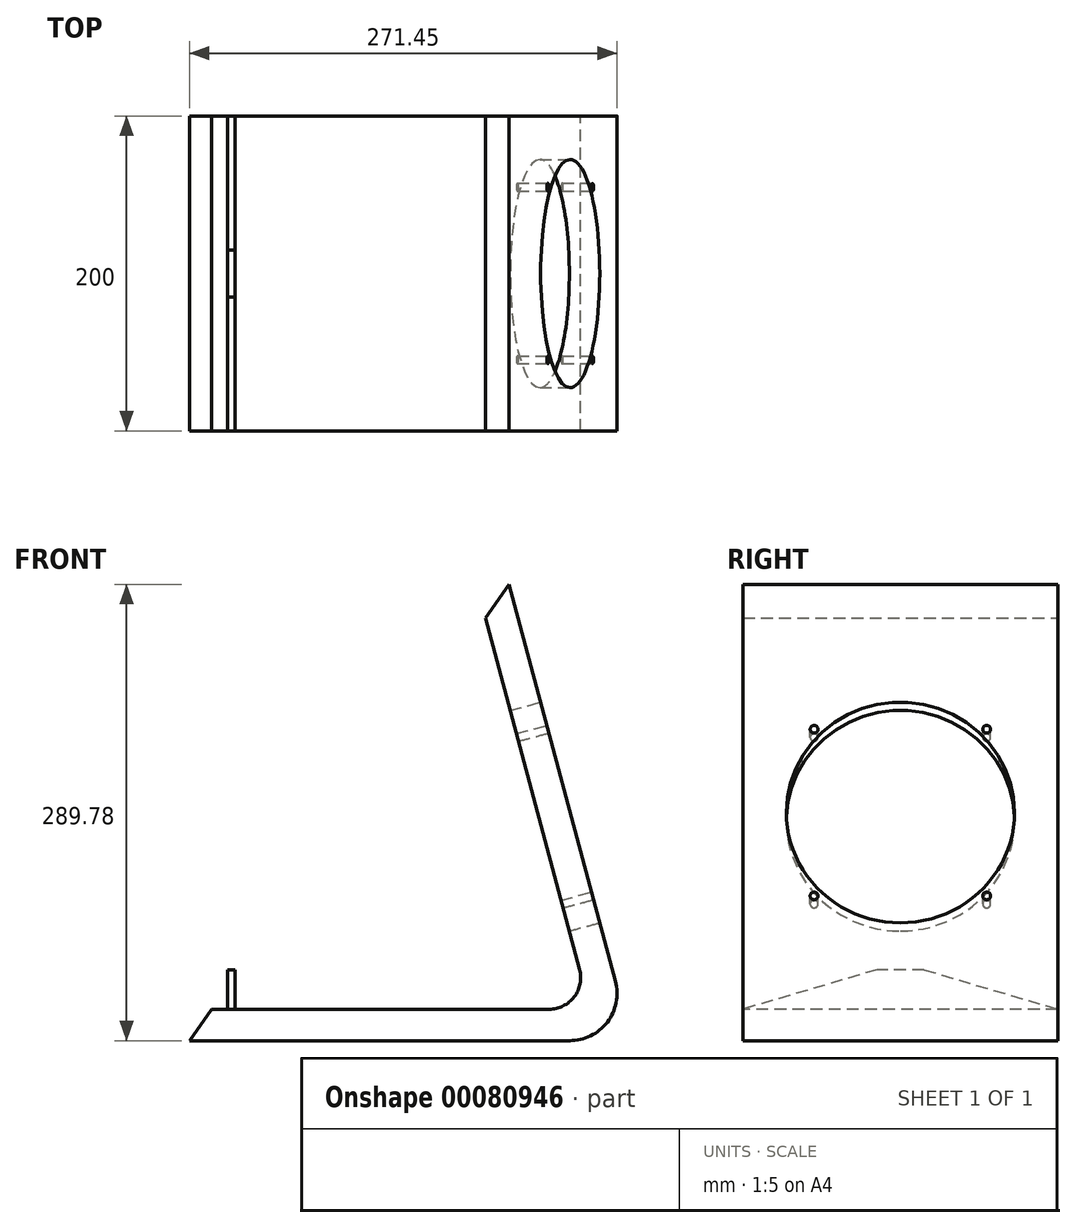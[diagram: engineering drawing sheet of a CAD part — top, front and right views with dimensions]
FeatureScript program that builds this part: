
annotation { "Feature Type Name" : "Feature", "Feature Type Description" : "" }
export const myFeature = defineFeature(function(context is Context, id is Id, definition is map)
    precondition{}
    {
        {
            var Q0;
            Q0=qCreatedBy(makeId("Front.planeOp"),FACE);
            var sketch = newSketch(context, id + "F0", { "sketchPlane" : qUnion([Q0])});
            skLineSegment(sketch, "E0", {"start": v(0, 0) * mm, "end": v(280.55, 0) * mm});
            skLineSegment(sketch, "E1", {"start": v(14, 20) * mm, "end": v(0, 0) * mm});
            skLineSegment(sketch, "E2", {"start": v(187.93, 268.4) * mm, "end": v(202.9, 289.78) * mm});
            skLineSegment(sketch, "E3", {"start": v(202.9, 289.78) * mm, "end": v(280.55, 0) * mm});
            skLineSegment(sketch, "E4", {"start": v(14, 20) * mm, "end": v(254.49, 20) * mm});
            skLineSegment(sketch, "E5", {"start": v(187.93, 268.4) * mm, "end": v(254.49, 20) * mm});
            skSolve(sketch);
        }
        {
            var Q0;
            Q0 = qSketchRegion(id + "F0", true);
            extrude(context, id + "F1", {"entities" : qUnion([Q0]), "depth" : 200 * mm});
        }
        {
            var Q0;
            Q0=makeQuery(id+"F1.opExtrude","SWEPT_FACE",FACE,{"disambiguationData":[OSD([sQuery(id+"F0.wireOp",EDGE,"E3")])]});
            var sketch = newSketch(context, id + "F2", { "sketchPlane" : qUnion([Q0])});
            skLineSegment(sketch, "E6", {"start": v(-100, 227.39) * mm, "end": v(-100, -72.61) * mm, "construction": true});
            skLineSegment(sketch, "E7", {"start": v(-200, 77.39) * mm, "end": v(0, 77.39) * mm, "construction": true});
            skCircle(sketch, "E8", {"center": v(-100, 77.39) * mm, "radius": 72.5 * mm});
            skLineSegment(sketch, "E9.bottom", {"start": v(-154.8, 132.19) * mm, "end": v(-45.2, 132.19) * mm, "construction": true});
            skLineSegment(sketch, "E9.top", {"start": v(-154.8, 22.59) * mm, "end": v(-45.2, 22.59) * mm, "construction": true});
            skLineSegment(sketch, "E9.left", {"start": v(-154.8, 132.19) * mm, "end": v(-154.8, 22.59) * mm, "construction": true});
            skLineSegment(sketch, "E9.right", {"start": v(-45.2, 132.19) * mm, "end": v(-45.2, 22.59) * mm, "construction": true});
            skCircle(sketch, "E10", {"center": v(-154.8, 132.19) * mm, "radius": 2.5 * mm});
            skCircle(sketch, "E11", {"center": v(-45.2, 132.19) * mm, "radius": 2.5 * mm});
            skCircle(sketch, "E12", {"center": v(-45.2, 22.59) * mm, "radius": 2.5 * mm});
            skCircle(sketch, "E13", {"center": v(-154.8, 22.59) * mm, "radius": 2.5 * mm});
            skSolve(sketch);
        }
        {
            var Q0;
            Q0 = qSketchRegion(id + "F2", true);
            var Q1;
            Q1=makeQuery(id+"F1.opExtrude","SWEPT_FACE",FACE,{"disambiguationData":[OSD([sQuery(id+"F0.wireOp",EDGE,"E5")])]});
            extrude(context, id + "F3", {"entities" : qUnion([Q0]), "operationType" : NewBodyOperationType.REMOVE, "endBound" : BoundingType.UP_TO_SURFACE, "oppositeDirection" : true, "endBoundEntityFace" : qUnion([Q1]), "depth" : 25 * mm});
        }
        {
            var Q0;
            Q0=makeQuery(id+"F1.opExtrude","SWEPT_EDGE",EDGE,{"disambiguationData":[OSD([sQuery(id+"F0.wireOp",EDGE,"E4"),sQuery(id+"F0.wireOp",EDGE,"E5")])]});
            fillet(context, id + "F4", {"entities" : qUnion([Q0]), "radius" : 20 * mm, "tangentPropagation" : true, "allowEdgeOverflow" : false});
        }
        {
            var Q0;
            Q0=makeQuery(id+"F1.opExtrude","SWEPT_EDGE",EDGE,{"disambiguationData":[OSD([sQuery(id+"F0.wireOp",EDGE,"E0"),sQuery(id+"F0.wireOp",EDGE,"E3")])]});
            fillet(context, id + "F5", {"entities" : qUnion([Q0]), "radius" : 30 * mm, "tangentPropagation" : true, "allowEdgeOverflow" : false});
        }
        {
            var Q0;
            Q0=makeQuery(id+"F1.opExtrude","SWEPT_FACE",FACE,{"disambiguationData":[OSD([sQuery(id+"F0.wireOp",EDGE,"E4")])]});
            var sketch = newSketch(context, id + "F6", { "sketchPlane" : qUnion([Q0])});
            skLineSegment(sketch, "E14.bottom", {"start": v(24, 0) * mm, "end": v(29, 0) * mm});
            skLineSegment(sketch, "E14.left", {"start": v(24, 0) * mm, "end": v(24, -200) * mm});
            skLineSegment(sketch, "E14.right", {"start": v(29, 0) * mm, "end": v(29, -200) * mm});
            skLineSegment(sketch, "E15", {"start": v(24, -200) * mm, "end": v(29, -200) * mm});
            skSolve(sketch);
        }
        {
            var Q0;
            Q0 = qSketchRegion(id + "F6", true);
            extrude(context, id + "F7", {"entities" : qUnion([Q0]), "operationType" : NewBodyOperationType.ADD, "depth" : 25 * mm});
        }
        {
            var Q0;
            Q0=makeQuery(id+"F7.opExtrude","SWEPT_FACE",FACE,{"disambiguationData":[OSD([sQuery(id+"F6.wireOp",EDGE,"E14.left")])]});
            var sketch = newSketch(context, id + "F8", { "sketchPlane" : qUnion([Q0])});
            skLineSegment(sketch, "E16", {"start": v(85, 45) * mm, "end": v(0, 20) * mm});
            skLineSegment(sketch, "E17", {"start": v(115, 45) * mm, "end": v(200, 20) * mm});
            skSolve(sketch);
        }
        {
            var Q0;
            Q0 = qSketchRegion(id + "F8", true);
            var Q1;
            {var subQ0=sQuery(id+"F8.wireOp",EDGE,"E16");Q1=makeQuery(id+"F8.imprint","IMPRINT",FACE,{"disambiguationData":[TD([[makeQuery(id+"F8.imprint","IMPRINT",EDGE,{"derivedFrom":subQ0}),-1.0]])]});}
            var Q2;
            {var subQ0=sQuery(id+"F8.wireOp",EDGE,"E17");Q2=makeQuery(id+"F8.imprint","IMPRINT",FACE,{"disambiguationData":[TD([[makeQuery(id+"F8.imprint","IMPRINT",EDGE,{"derivedFrom":subQ0}),1.0]])]});}
            extrude(context, id + "F9", {"entities" : qUnion([Q0, Q1, Q2]), "operationType" : NewBodyOperationType.REMOVE, "oppositeDirection" : true, "depth" : 25 * mm});
        }
    });
